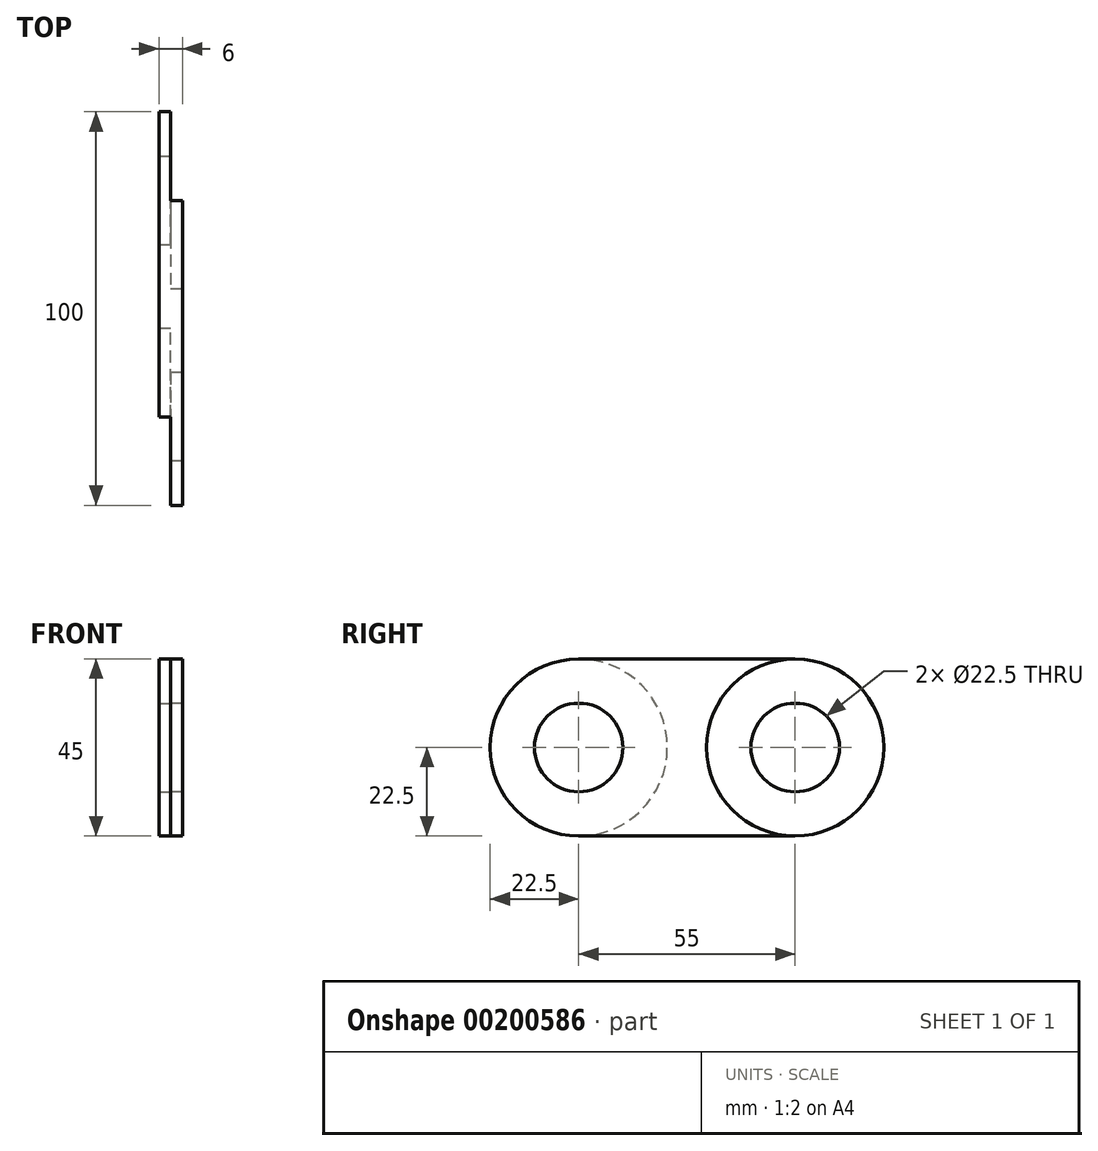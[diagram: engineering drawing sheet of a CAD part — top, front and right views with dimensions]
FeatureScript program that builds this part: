
annotation { "Feature Type Name" : "Feature", "Feature Type Description" : "" }
export const myFeature = defineFeature(function(context is Context, id is Id, definition is map)
    precondition{}
    {
        {
            var Q0;
            Q0=qCreatedBy(makeId("Right.planeOp"),FACE);
            var sketch = newSketch(context, id + "F0", { "sketchPlane" : qUnion([Q0])});
            skCircle(sketch, "E0", {"center": v(0, 0) * mm, "radius": 22.5 * mm});
            skCircle(sketch, "E1", {"center": v(55, 0) * mm, "radius": 22.5 * mm});
            skLineSegment(sketch, "E2", {"start": v(0, 22.5) * mm, "end": v(55, 22.5) * mm});
            skCircle(sketch, "E3", {"center": v(0, 0) * mm, "radius": 11.25 * mm});
            skCircle(sketch, "E4", {"center": v(55, 0) * mm, "radius": 11.25 * mm});
            skLineSegment(sketch, "E5", {"start": v(0, -22.5) * mm, "end": v(55, -22.5) * mm});
            skSolve(sketch);
        }
        {
            var Q0;
            {var subQ0=sQuery(id+"F0.wireOp",EDGE,"E2");Q0=makeQuery(id+"F0.imprint","IMPRINT",FACE,{"disambiguationData":[TD([[makeQuery(id+"F0.imprint","IMPRINT",EDGE,{"derivedFrom":subQ0}),-1.0]])]});}
            extrude(context, id + "F1", {"entities" : qUnion([Q0]), "depth" : 3 * mm, "hasSecondDirection" : true, "secondDirectionOppositeDirection" : true, "secondDirectionDepth" : 3 * mm});
        }
        {
            var Q0;
            Q0=makeQuery(id+"F0.imprint","IMPRINT",FACE,{"disambiguationData":[TD([[makeQuery(id+"F0.imprint","IMPRINT",EDGE,{"derivedFrom":sQuery(id+"F0.wireOp",EDGE,"E3")}),-1.0]])]});
            extrude(context, id + "F2", {"entities" : qUnion([Q0]), "operationType" : NewBodyOperationType.ADD, "depth" : 3 * mm});
        }
        {
            var Q0;
            Q0=makeQuery(id+"F0.imprint","IMPRINT",FACE,{"disambiguationData":[TD([[makeQuery(id+"F0.imprint","IMPRINT",EDGE,{"derivedFrom":sQuery(id+"F0.wireOp",EDGE,"E4")}),-1.0]])]});
            extrude(context, id + "F3", {"entities" : qUnion([Q0]), "operationType" : NewBodyOperationType.ADD, "oppositeDirection" : true, "depth" : 3 * mm});
        }
    });
